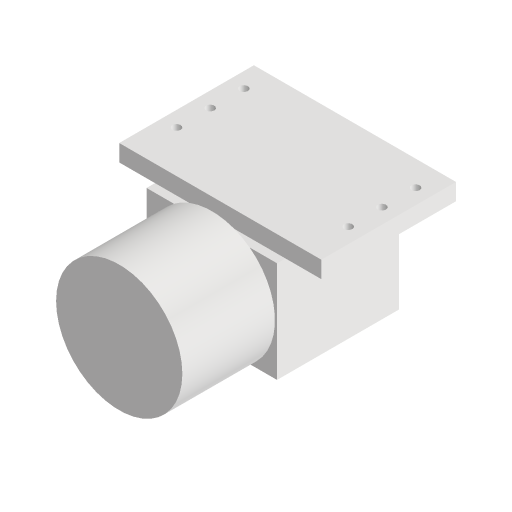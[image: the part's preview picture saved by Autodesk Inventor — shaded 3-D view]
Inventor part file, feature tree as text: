
AUTODESK INVENTOR PART (.ipt)
format: ipt  version: 2024.1 (Build 281209000, 209)  size: 156,160 bytes
history: native  units: mm
features: extrude x5, sketch x5, projected_geometry x3
ambient origin geometry x8: Origin, YZ Plane, XZ Plane, XY Plane, X Axis, Y Axis, Z Axis, Center Point
bodies: Volumenkörper1 (feature_tree)
feature tree (13):
  extrude  "Extrusion1"  Depth=14.5mm
  extrude  "Extrusion2"  Depth=24.0mm
  extrude  "Extrusion3"  Depth=2.5mm
  extrude  "Extrusion4"  Depth=2.0mm
  extrude  "Extrusion5"  Depth=7.0mm TaperAngle=0.0deg
  sketch  "Skizze1"  dims[d0=15.5mm d1=14.5mm]
  sketch  "Skizze2"  dims[d2=12.0mm d3=0.0mm d4=24.0mm]
  sketch  "Skizze3"  dims[d5=16.0mm d6=2.5mm]
  projected_geometry  "Projizierte Kontur1"
  sketch  "Skizze4"  dims[d7=2.0mm d8=0.0mm d9=3.0mm]
  projected_geometry  "Projizierte Kontur2"
  sketch  "Skizze5"  dims[d10=1.124503mm d11=7.0mm d12=0.0mm d13=15.0mm d14=11.0mm d15=0.0mm d16=1.0mm d17=1.0mm d18=1.0mm d19=5.0mm d20=4.0mm d21=4.0mm d22=1.8mm d23=1.8mm d24=1.8mm d25=11.0mm d26=0.0mm]
  projected_geometry  "Projizierte Kontur3"
